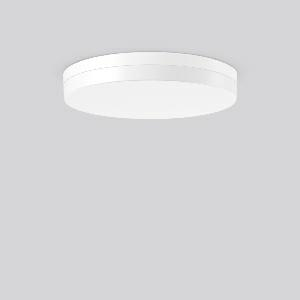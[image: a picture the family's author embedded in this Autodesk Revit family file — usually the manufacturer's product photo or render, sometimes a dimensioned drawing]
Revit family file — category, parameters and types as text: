
# Revit family: flat_slim_round_312634_002_76_748a
name_source: partatom
category: Lighting Fixtures
units: mm (PartAtom-declared; Revit-internal decimal feet)

## family parameters
Cut with Voids When Loaded = No
Host = Face
Light Source = No
Part Type = Normal
Room Calculation Point = No
Round Connector Dimension = Use Diameter
Shared = No

## types (1)
- MultiLumen 1 830 (1 x LED Modul 830, 3450 lm, 3000)
    Apparent Load = 26 VA
    CIE Flux Codes = 40 71 90 84 100
    Color Rendering = 80
    Color Temperature = 3000
    Default Elevation = 1800 mm
    Height = 70 mm
    Lamp = 1 x LED Modul 830
    Lamp Light Flux = 3450 lm
    Lamp count = 1
    Length = 480 mm
    Lifetime = 50000 h
    Luminous efficacy = 133 lm/W
    Manufacturer = RZB
    ModVariant = No
    Model = 312634.002.76
    Mounting Place = Ceiling
    Mounting Type = Surface mounted
    Number of Poles = 1
    OnlyDefault = Yes
    Power Factor = 1
    Product Name = FLAT SLIM round
    Product group = Surface mounted ceiling and wall luminaires
    ProductGroupID = 305
    Protection Class = Protection class I
    Protection Degree = Degree of protection
    RLX_Detail_Level = 1
    RLX_Emergency_Light_Flux = 0 lm
    RLX_Emergency_Type = 0
    RLX_Emergency_Type_DB = No
    RlxData = <blob elided: 21293 chars, md5=b94c7810>
    Socket = socket
    Standby Power = 0 W
    System Light Flux = 3450 lm
    System Power = 26 W
    Type Comments = MultiLumen 1 830
    Type Image = 312633.002.jpg
    URL = http://relux.com
    VarID = multilumen_1_830
    Voltage = 0 V
    Weight = 0.00 kg
    Width = 0 mm  [stored 0 ft]

note: [stored X ft] marks values corroborated as IEEE doubles in the binary element streams (Revit-internal decimal feet)

## geometry (parser evidence)
native form markers: Blend x4, Sweep x13
no freeform markers — native parametric forms only
